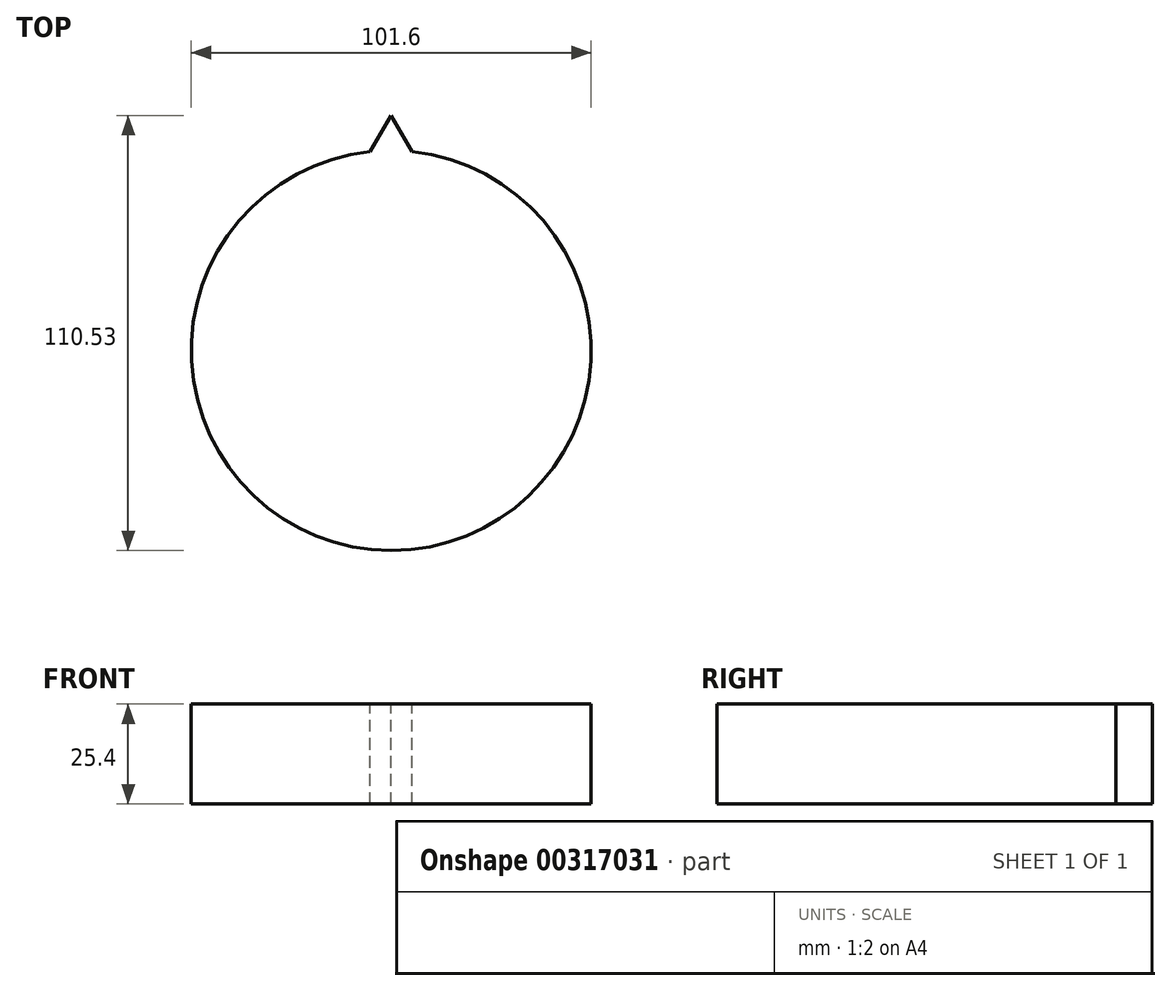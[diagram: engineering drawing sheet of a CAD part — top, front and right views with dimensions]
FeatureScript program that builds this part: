
annotation { "Feature Type Name" : "Feature", "Feature Type Description" : "" }
export const myFeature = defineFeature(function(context is Context, id is Id, definition is map)
    precondition{}
    {
        {
            var Q0;
            Q0=qCreatedBy(makeId("Top.planeOp"),FACE);
            var sketch = newSketch(context, id + "F0", { "sketchPlane" : qUnion([Q0])});
            skCircle(sketch, "E0", {"center": v(0, 0) * mm, "radius": 50.8 * mm});
            skSolve(sketch);
        }
        {
            var Q0;
            Q0 = qSketchRegion(id + "F0", true);
            extrude(context, id + "F1", {"entities" : qUnion([Q0]), "depth" : 25.4 * mm, "symmetric" : true});
        }
        {
            var Q0;
            Q0=makeQuery(id+"F1.opExtrude","CAP_FACE",FACE,{"disambiguationData":[OSD([sQuery(id+"F0.wireOp",EDGE,"E0")])],"isStart":false});
            var sketch = newSketch(context, id + "F2", { "sketchPlane" : qUnion([Q0])});
            skLineSegment(sketch, "E1", {"start": v(0, 59.73) * mm, "end": v(-5.32, 50.52) * mm});
            skLineSegment(sketch, "E2", {"start": v(-5.32, 50.52) * mm, "end": v(5.32, 50.52) * mm});
            skLineSegment(sketch, "E3", {"start": v(0, 59.73) * mm, "end": v(5.32, 50.52) * mm});
            skSolve(sketch);
        }
        {
            var Q0;
            Q0 = qSketchRegion(id + "F2", true);
            extrude(context, id + "F3", {"entities" : qUnion([Q0]), "operationType" : NewBodyOperationType.ADD, "oppositeDirection" : true, "depth" : 25.4 * mm});
        }
    });
